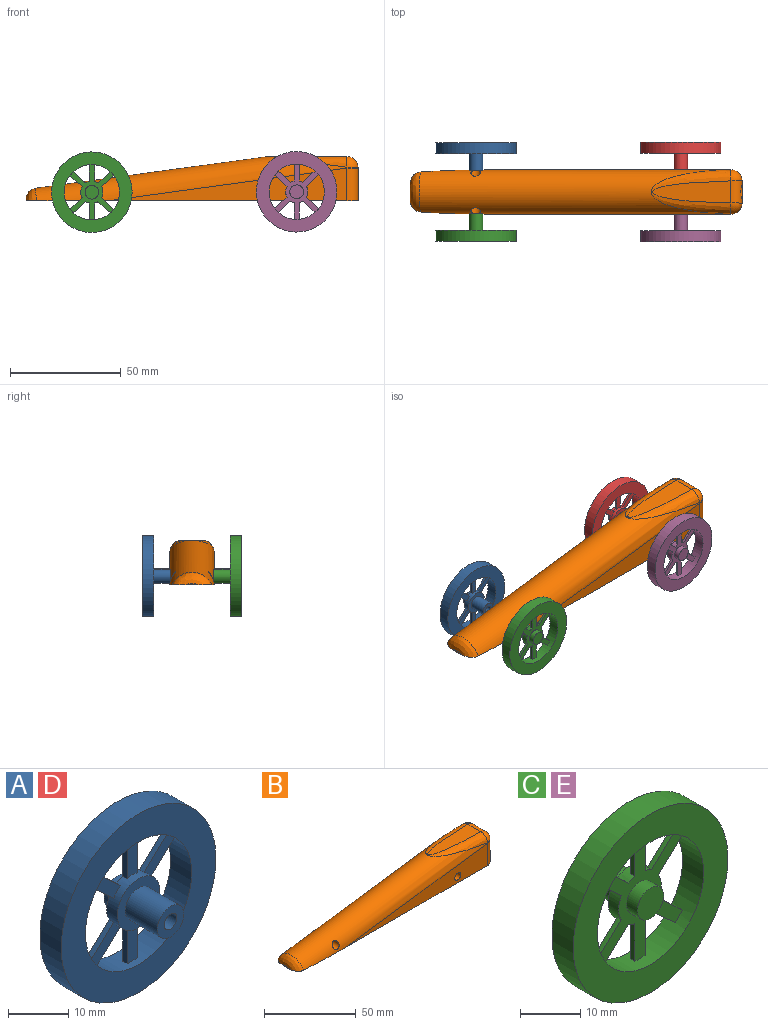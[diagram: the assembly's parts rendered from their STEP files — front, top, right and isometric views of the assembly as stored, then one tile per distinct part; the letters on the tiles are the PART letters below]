
ASSEMBLY  parts=5 mates=4
PART A: 31 faces, bbox 36.4x12.5x36.4 mm
  f0: cylinder r=3.1mm len=7.5mm, axis (0,-1,0), area 146.1mm2, adj f2,f5
  f1: cylinder r=1.5mm len=10mm, axis (0,-1,0), area 94.2mm2, adj f2,f3
  f2: plane 6.2x6.2mm, normal (0,-1,0), area 23.1mm2, adj f0,f1
  f3: plane 3x3mm, normal (0,-1,0), area 7.1mm2, adj f1
  f4: cylinder r=5mm len=10mm, axis (0,1,0), area 64mm2, adj f5,f6,f9,f10,f11,f12,f13,f14
  f5: plane 10x10mm, normal (0,-1,0), area 48.3mm2, adj f0,f4
  f6: plane 25.02x19.87mm, normal (0,1,0), area 156.8mm2, adj f4,f8,f9,f10,f12,f13,f15,f16
  f7: plane 6.18x6.18mm, normal (0,1,0), area 30mm2, adj f8
  f8: cylinder r=3.09mm len=6.18mm, axis (0,-1,0), area 48.5mm2, adj f6,f7
  f9: plane 5.55x5.17mm, normal (0.68,0,-0.73), area 7.6mm2, adj f4,f6,f11,f27
  f10: plane 5.55x5.17mm, normal (-0.68,0,0.73), area 7.6mm2, adj f4,f6,f11,f27
  f11: plane 7.19x6.93mm, normal (0,-1,0), area 18.1mm2, adj f4,f9,f10,f27
  f12: plane 7.59x1mm, normal (1,0,0), area 7.6mm2, adj f4,f6,f14,f27
  f13: plane 7.59x1mm, normal (-1,0,0), area 7.6mm2, adj f4,f6,f14,f27
  f14: plane 7.65x2.4mm, normal (0,-1,0), area 18.1mm2, adj f4,f12,f13,f27
  f15: plane 5.55x5.17mm, normal (-0.68,0,-0.73), area 7.6mm2, adj f4,f6,f17,f27
  f16: plane 5.55x5.17mm, normal (0.68,0,0.73), area 7.6mm2, adj f4,f6,f17,f27
  f17: plane 7.19x6.93mm, normal (0,-1,0), area 18.1mm2, adj f4,f15,f16,f27
  f18: plane 5.55x5.17mm, normal (-0.68,0,0.73), area 7.6mm2, adj f4,f6,f20,f27
  f19: plane 5.55x5.17mm, normal (0.68,0,-0.73), area 7.6mm2, adj f4,f6,f20,f27
  f20: plane 7.19x6.93mm, normal (0,-1,0), area 18.1mm2, adj f4,f18,f19,f27
  f21: plane 7.59x1mm, normal (-1,0,0), area 7.6mm2, adj f4,f6,f23,f27
  f22: plane 7.59x1mm, normal (1,0,0), area 7.6mm2, adj f4,f6,f23,f27
  f23: plane 7.65x2.4mm, normal (0,-1,0), area 18.1mm2, adj f4,f21,f22,f27
  f24: plane 5.55x5.17mm, normal (-0.68,0,-0.73), area 7.6mm2, adj f4,f6,f26,f27
  f25: plane 5.55x5.17mm, normal (0.68,0,0.73), area 7.6mm2, adj f4,f6,f26,f27
  f26: plane 7.19x6.93mm, normal (0,-1,0), area 18.1mm2, adj f4,f24,f25,f27
  f27: cylinder r=12.5mm len=25mm, axis (0,-1,0), area 378.3mm2, adj f6,f9,f10,f11,f12,f13,f14,f15
  f28: cylinder r=18.2mm len=36.4mm, axis (0,-1,0), area 571.8mm2, adj f29,f30
  f29: plane 36.4x36.4mm, normal (0,1,0), area 549.7mm2, adj f27,f28
  f30: plane 36.4x36.4mm, normal (0,-1,0), area 549.7mm2, adj f27,f28
PART B: 22 faces, bbox 153x23x31.9 mm
  f0: plane 12.44x10mm, normal (1,0,0), area 85.1mm2, adj f7,f8,f13,f19
  f1: plane 2.57x0.71mm, normal (1,0,0), area 0.6mm2, adj f8,f13,f14,f17
  f2: plane 108.36x14.77mm, normal (0,1,0), area 784.5mm2, adj f7,f11,f12,f13
  f3: plane 108.36x14.77mm, normal (0,-1,0), area 784.5mm2, adj f7,f11,f12,f19
  f4: plane 5.19x0.73mm, normal (-1,0,0), area 2.6mm2, adj f7,f21
  f5: plane 2.57x0.71mm, normal (1,0,0), area 0.6mm2, adj f8,f17,f19,f20
  f6: plane 35.35x9.99mm, normal (0,0,1), area 274.1mm2, adj f16,f17
  f7: plane 152.96x22.96mm, normal (0,0,-1), area 2947.4mm2, adj f0,f2,f3,f4,f12,f13,f19,f21
  f8: cylinder r=5mm len=50mm, axis (1,0,0), area 1570.8mm2, adj f0,f1,f5,f9,f17
  f9: plane 10x10mm, normal (1,0,0), area 78.5mm2, adj f8
  f10: cylinder r=2.25mm len=19.34mm, axis (0,1,0), area 242.3mm2, adj f12
  f11: cylinder r=2.25mm len=20mm, axis (0,1,0), area 282.7mm2, adj f2,f3
  f12: cylinder r=10mm len=141.09mm, axis (0.99,0,0.14), area 3566.8mm2, adj f2,f3,f7,f10,f14,f16,f20,f21
  f13: cylinder r=5mm len=14.77mm, axis (0,0,-1), area 116mm2, adj f0,f1,f2,f7,f14
  f14: bspline ~5.12x5.11mm, area 2.9mm2, adj f1,f12,f13,f15
  f15: sphere r=5mm, area 38.5mm2, adj f14,f16,f17
  f16: bspline ~36.01x19.98mm, area 357mm2, adj f6,f12,f15,f18
  f17: cylinder r=5mm len=9.99mm, axis (0,-1,0), area 63.2mm2, adj f1,f5,f6,f8,f15,f18
  f18: sphere r=5mm, area 38.3mm2, adj f16,f17,f20
  f19: cylinder r=5mm len=14.77mm, axis (0,0,1), area 116mm2, adj f0,f3,f5,f7,f20
  f20: bspline ~5.03x5.01mm, area 2.9mm2, adj f5,f12,f18,f19
  f21: bspline ~18.04x7.82mm, area 101.4mm2, adj f4,f7,f12
PART C: 31 faces, bbox 36.4x12.5x36.4 mm
  f0: cylinder r=3.1mm len=7.5mm, axis (0,1,0), area 146.1mm2, adj f2,f5
  f1: cylinder r=1.5mm len=10mm, axis (0,1,0), area 94.2mm2, adj f2,f3
  f2: plane 6.2x6.2mm, normal (0,1,0), area 23.1mm2, adj f0,f1
  f3: plane 3x3mm, normal (0,1,0), area 7.1mm2, adj f1
  f4: cylinder r=5mm len=10mm, axis (0,-1,0), area 64mm2, adj f5,f6,f9,f10,f11,f12,f13,f14
  f5: plane 10x10mm, normal (0,1,0), area 48.3mm2, adj f0,f4
  f6: plane 25.02x19.87mm, normal (0,-1,0), area 156.8mm2, adj f4,f8,f9,f10,f12,f13,f15,f16
  f7: plane 6.18x6.18mm, normal (0,-1,0), area 30mm2, adj f8
  f8: cylinder r=3.09mm len=6.18mm, axis (0,1,0), area 48.5mm2, adj f6,f7
  f9: plane 5.55x5.17mm, normal (0.68,0,-0.73), area 7.6mm2, adj f4,f6,f11,f27
  f10: plane 5.55x5.17mm, normal (-0.68,0,0.73), area 7.6mm2, adj f4,f6,f11,f27
  f11: plane 7.19x6.93mm, normal (0,1,0), area 18.1mm2, adj f4,f9,f10,f27
  f12: plane 7.59x1mm, normal (1,0,0), area 7.6mm2, adj f4,f6,f14,f27
  f13: plane 7.59x1mm, normal (-1,0,0), area 7.6mm2, adj f4,f6,f14,f27
  f14: plane 7.65x2.4mm, normal (0,1,0), area 18.1mm2, adj f4,f12,f13,f27
  f15: plane 5.55x5.17mm, normal (-0.68,0,-0.73), area 7.6mm2, adj f4,f6,f17,f27
  f16: plane 5.55x5.17mm, normal (0.68,0,0.73), area 7.6mm2, adj f4,f6,f17,f27
  f17: plane 7.19x6.93mm, normal (0,1,0), area 18.1mm2, adj f4,f15,f16,f27
  f18: plane 5.55x5.17mm, normal (-0.68,0,0.73), area 7.6mm2, adj f4,f6,f20,f27
  f19: plane 5.55x5.17mm, normal (0.68,0,-0.73), area 7.6mm2, adj f4,f6,f20,f27
  f20: plane 7.19x6.93mm, normal (0,1,0), area 18.1mm2, adj f4,f18,f19,f27
  f21: plane 7.59x1mm, normal (-1,0,0), area 7.6mm2, adj f4,f6,f23,f27
  f22: plane 7.59x1mm, normal (1,0,0), area 7.6mm2, adj f4,f6,f23,f27
  f23: plane 7.65x2.4mm, normal (0,1,0), area 18.1mm2, adj f4,f21,f22,f27
  f24: plane 5.55x5.17mm, normal (-0.68,0,-0.73), area 7.6mm2, adj f4,f6,f26,f27
  f25: plane 5.55x5.17mm, normal (0.68,0,0.73), area 7.6mm2, adj f4,f6,f26,f27
  f26: plane 7.19x6.93mm, normal (0,1,0), area 18.1mm2, adj f4,f24,f25,f27
  f27: cylinder r=12.5mm len=25mm, axis (0,1,0), area 378.3mm2, adj f6,f9,f10,f11,f12,f13,f14,f15
  f28: cylinder r=18.2mm len=36.4mm, axis (0,1,0), area 571.8mm2, adj f29,f30
  f29: plane 36.4x36.4mm, normal (0,-1,0), area 549.7mm2, adj f27,f28
  f30: plane 36.4x36.4mm, normal (0,1,0), area 549.7mm2, adj f27,f28
PART D: same geometry as A
PART E: same geometry as C
PLACE A t=(-51.94,55.18,6.93)mm
PLACE B t=(-59.81,60.39,3.04)mm
PLACE C t=(-51.94,60.6,6.93)mm
PLACE D t=(40.6,55.39,7.13)mm
PLACE E t=(40.6,60.39,7.13)mm
MATE revolute D.f0 <-> B.f11  axis (0,-1,0) through (40.6,80.39,7.13)mm
MATE revolute A.f0 <-> B.f10  axis (0,-1,0) through (-51.94,80.18,6.93)mm
MATE revolute E.f0 <-> B.f11  axis (0,1,0) through (40.6,60.39,7.13)mm
MATE revolute C.f0 <-> B.f10  axis (0,1,0) through (-51.94,60.6,6.93)mm
